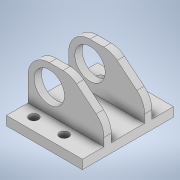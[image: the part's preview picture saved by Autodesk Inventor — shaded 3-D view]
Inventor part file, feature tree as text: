
AUTODESK INVENTOR PART (.ipt)
format: ipt  version: 2022 (Build 260153000, 153)  size: 184,832 bytes
history: native  units: mm
features: extrude x3, sketch x3, projected_geometry x2, fillet x1
ambient origin geometry x8: Origin, YZ Plane, XZ Plane, XY Plane, X Axis, Y Axis, Z Axis, Center Point
bodies: Solid1 (feature_tree)
feature tree (9):
  extrude  "Extrusion1"  Depth=25.0mm
  extrude  "Extrusion2"  Depth=10.0mm
  extrude  "Extrusion3"  Depth=7.0mm
  fillet  "Fillet1"  Radius=25.5mm
  sketch  "Sketch1"  dims[d0=30.0mm d1=25.0mm]
  sketch  "Sketch2"  dims[d2=3.0mm d3=20.0mm d5=22.0mm d6=20.0mm d8=10.0mm]
  projected_geometry  "Projected Loop1"
  sketch  "Sketch3"  dims[d11=20.0mm d12=4.0mm d13=25.5mm d14=0.0mm d15=3.0mm d16=3.0mm d17=3.0mm d19=11.0mm d20=2.4mm d21=2.4mm d22=7.1mm d23=25.5mm d24=0.0mm d25=8.0mm d26=7.0mm d27=7.0mm d28=14.0mm d29=6.0mm d30=10.0mm d31=25.5mm d32=0.0mm d33=7.0mm]
  projected_geometry  "Projected Loop2"
